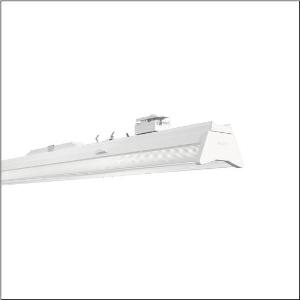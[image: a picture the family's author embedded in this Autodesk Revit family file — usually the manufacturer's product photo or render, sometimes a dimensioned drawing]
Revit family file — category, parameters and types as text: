
# Revit family: licross_r__21_performance_ho_52tm16cn4c5m_51b1
name_source: partatom
category: Lighting Fixtures
units: mm (PartAtom-declared; Revit-internal decimal feet)

## family parameters
Cut with Voids When Loaded = No
Host = Face
Light Source = No
Part Type = Normal
Room Calculation Point = No
Round Connector Dimension = Use Diameter
Shared = No

## types (1)
- --- (1 x LED, 12610 lm, 68.9 W, 4000K)
    Apparent Load = 69 VA
    CIE Flux Codes = 63 87 95 78 100
    Color Rendering = 80
    Color Temperature = 4000K
    Default Elevation = 1800 mm
    Description = Licross® 21 Performance HO, luminaire insert, of sheet steel, galvanised, coil coated, white, length: 1.500mm, width: 120mm, height: 123mm, LED rated luminous flux: 12.610lm, light colour: 840, SDCM (Standard Deviation of Colour Matching)MacAdam ≤ 3 SDCM (initial), control gear: ON/OFF Multilumen, CLOi, with plug, 3-pole, with phase selection, mains connection: 220..240V, AC, 50/60Hz, start of lifetime: 69W, end of service life: 83W, internal wiring halogen-free, primary light control with lens, of plastic, primary optical cover: cover, of PMMA, light emission: direct/indirect distribution, primary light characteristic: symmetric, protection rating (complete): IP40, insulation class (complete): insulation class I (protective earthing), certification: CE, ENEC, UKCA, protection symbol: D if used in an environment without relevant dust loads with corresponding accessories, impact resistance: IK06, permissible ambient temperature for indoor applications: -35..+35°C, corresponds to IFS (International Featured Standards) requirements for safety and quality in the food industry, reducing of maximum allowable ambient temperature of 5°C with ceiling mounting, LABS conformity tested according to VDMA 24364:2018-05, packaging unit: 1 piece
    Height = 114 mm
    Lamp = 1 x LED
    Lamp Light Flux = 12610 lm
    Lamp Power = 68.9 W
    Lamp count = 1
    Length = 1500 mm
    Luminous efficacy = 183 lm/W
    Manufacturer = Siteco
    ModVariant = No
    Model = 52TM16CN4C5M
    Mounting Place = Ceiling
    Mounting Type = Pendant
    Number of Poles = 1
    OnlyDefault = Yes
    Power Factor = 1
    Product Name = Licross® 21 Performance HO
    Product group = luminaire insert | ceiling pendant
    ProductGroupID = 901
    Protection Class = Protection class I
    Protection Degree = IP 40
    RLX_Detail_Level = 1
    RLX_Emergency_Light_Flux = 0 lm
    RLX_Emergency_Type = 0
    RLX_Emergency_Type_DB = No
    RlxData = <blob elided: 31973 chars, md5=2ca1da50>
    Socket = socket
    Standby Power = 0 W
    System Light Flux = 12610 lm
    System Power = 69 W
    Type Comments = factory setting: luminous flux: 100 % | (A | C | E) | 162 mA
    Type Image = l_1256138.jpg
    URL = http://relux.com
    VarID = @adj_115535
    Voltage = 0 V
    Weight = 0.00 kg
    Width = 120 mm

## geometry (parser evidence)
native form markers: Blend x4, Sweep x10
no freeform markers — native parametric forms only
